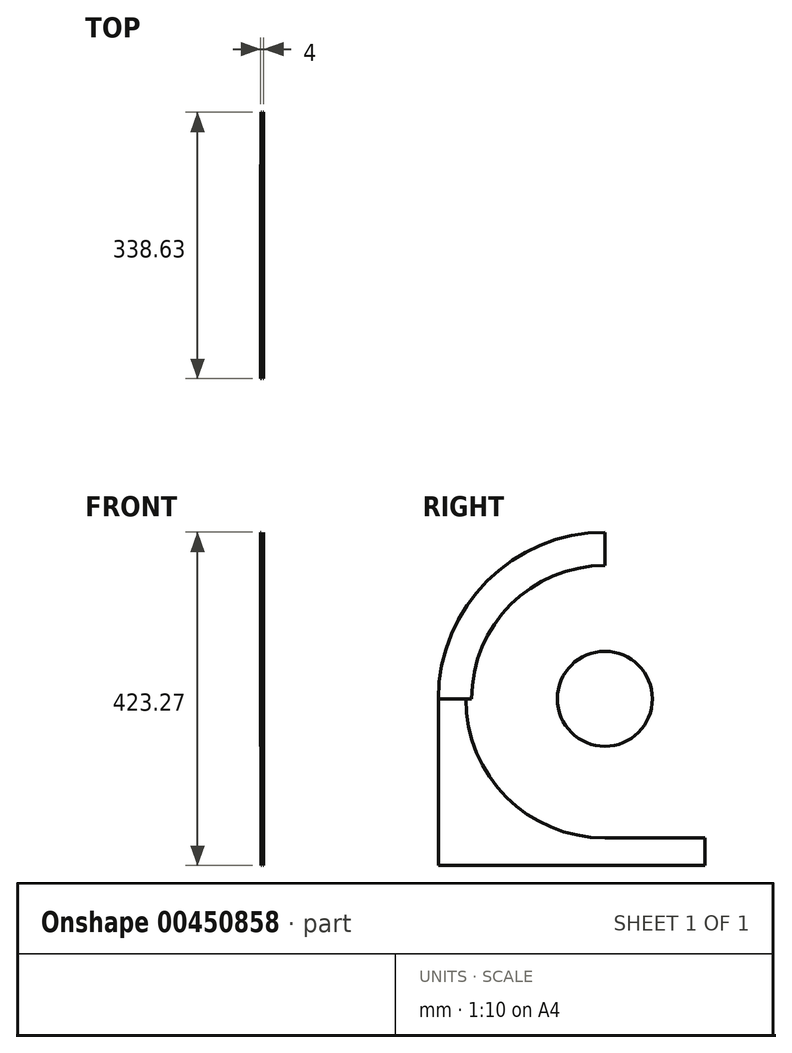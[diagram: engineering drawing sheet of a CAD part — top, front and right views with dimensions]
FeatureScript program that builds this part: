
annotation { "Feature Type Name" : "Feature", "Feature Type Description" : "" }
export const myFeature = defineFeature(function(context is Context, id is Id, definition is map)
    precondition{}
    {
        {
            assignVariable(context, id + "F0", {"name" : "trw", "anyValue" : .5});
        }
        {
            assignVariable(context, id + "F1", {"name" : "trsp", "anyValue" : 2});
        }
        {
            assignVariable(context, id + "F2", {"name" : "shwhw", "anyValue" : 1});
        }
        {
            var Q0;
            Q0=qCreatedBy(makeId("Right.planeOp"),FACE);
            cPlane(context, id + "F3", {"entities" : qUnion([Q0]), "cplaneType" : CPlaneType.OFFSET, "offset" : (getVariable(context, 'trsp') / 2) * mm, "width" : 152.4 * mm, "height" : 152.4 * mm});
        }
        {
            var Q0;
            Q0=qCreatedBy(id+"F3.planeOp",FACE);
            var sketch = newSketch(context, id + "F4", { "sketchPlane" : qUnion([Q0])});
            skLineSegment(sketch, "E0.bottom", {"start": v(0, 0) * mm, "end": v(127, 0) * mm});
            skLineSegment(sketch, "E0.top", {"start": v(0, 34.93) * mm, "end": v(127, 34.93) * mm});
            skLineSegment(sketch, "E0.left", {"start": v(0, 0) * mm, "end": v(0, 34.93) * mm});
            skLineSegment(sketch, "E0.right", {"start": v(127, 0) * mm, "end": v(127, 34.92) * mm});
            skCircle(sketch, "E1", {"center": v(0, 211.63) * mm, "radius": 60.33 * mm});
            skArc(sketch, "E2", {"start": v(-176.7, 211.63) * mm, "mid": v(-124.95, 86.68) * mm, "end": v(0, 34.93) * mm});
            skArc(sketch, "E3", {"start": v(-211.63, 211.63) * mm, "mid": v(-149.65, 61.99) * mm, "end": v(0, 0) * mm});
            skLineSegment(sketch, "E4", {"start": v(-176.7, 211.63) * mm, "end": v(-211.63, 211.63) * mm});
            skLineSegment(sketch, "E5", {"start": v(0, 0) * mm, "end": v(-211.63, 0) * mm});
            skLineSegment(sketch, "E6", {"start": v(-211.63, 0) * mm, "end": v(-211.63, 211.63) * mm});
            skSolve(sketch);
        }
        {
            var Q0;
            Q0=makeQuery(id+"F4.imprint","IMPRINT",FACE,{"disambiguationData":[TD([[makeQuery(id+"F4.imprint","IMPRINT",EDGE,{"derivedFrom":sQuery(id+"F4.wireOp",EDGE,"E1")}),1.0]])]});
            extrude(context, id + "F5", {"entities" : qUnion([Q0]), "depth" : (getVariable(context, 'shwhw')) * mm});
        }
        {
            var Q0;
            Q0=makeQuery(id+"F4.imprint","IMPRINT",FACE,{"disambiguationData":[TD([[makeQuery(id+"F4.imprint","IMPRINT",EDGE,{"derivedFrom":sQuery(id+"F4.wireOp",EDGE,"E0.left")}),1.0]])]});
            var Q1;
            Q1=makeQuery(id+"F4.imprint","IMPRINT",FACE,{"disambiguationData":[TD([[makeQuery(id+"F4.imprint","IMPRINT",EDGE,{"derivedFrom":sQuery(id+"F4.wireOp",EDGE,"E0.bottom")}),1.0]])]});
            extrude(context, id + "F6", {"entities" : qUnion([Q0, Q1]), "depth" : (getVariable(context, 'trw')) * mm});
        }
        {
            var Q0;
            Q0=makeQuery(id+"F4.imprint","IMPRINT",FACE,{"disambiguationData":[TD([[makeQuery(id+"F4.imprint","IMPRINT",EDGE,{"derivedFrom":sQuery(id+"F4.wireOp",EDGE,"E3")}),-1.0]])]});
            extrude(context, id + "F7", {"entities" : qUnion([Q0]), "operationType" : NewBodyOperationType.ADD, "depth" : (getVariable(context, 'trw')) * mm});
        }
        {
            var Q0;
            Q0=qCreatedBy(makeId("Right.planeOp"),FACE);
            cPlane(context, id + "F8", {"entities" : qUnion([Q0]), "cplaneType" : CPlaneType.OFFSET, "offset" : (getVariable(context, 'trsp') / 2 + getVariable(context, 'trw')) * mm, "width" : 152.4 * mm, "height" : 152.4 * mm});
        }
        {
            var Q0;
            Q0=qCreatedBy(id+"F8.planeOp",FACE);
            var sketch = newSketch(context, id + "F9", { "sketchPlane" : qUnion([Q0])});
            skCircle(sketch, "E7.0.0", {"center": v(0, 211.63) * mm, "radius": 60.33 * mm});
            skArc(sketch, "E8", {"start": v(0, 380.95) * mm, "mid": v(-119.72, 331.36) * mm, "end": v(-169.32, 211.63) * mm});
            skArc(sketch, "E9", {"start": v(0, 423.27) * mm, "mid": v(-149.65, 361.28) * mm, "end": v(-211.63, 211.63) * mm});
            skLineSegment(sketch, "E10", {"start": v(0, 423.27) * mm, "end": v(0, 380.95) * mm});
            skLineSegment(sketch, "E11", {"start": v(-169.32, 211.63) * mm, "end": v(-220.4, 211.63) * mm});
            skSolve(sketch);
        }
        {
            var Q0;
            {var subQ0=sQuery(id+"F9.wireOp",EDGE,"E8");Q0=makeQuery(id+"F9.imprint","IMPRINT",FACE,{"disambiguationData":[TD([[makeQuery(id+"F9.imprint","IMPRINT",EDGE,{"derivedFrom":subQ0}),-1.0]])]});}
            extrude(context, id + "F10", {"entities" : qUnion([Q0]), "depth" : (getVariable(context, 'trw')) * mm});
        }
        {
            var Q0;
            Q0=makeQuery(id+"F10.opExtrude","SWEPT_BODY",BODY,{"disambiguationData":[OSD([sQuery(id+"F9.wireOp",EDGE,"E8"),sQuery(id+"F9.wireOp",EDGE,"E9"),sQuery(id+"F9.wireOp",EDGE,"E10"),sQuery(id+"F9.wireOp",EDGE,"E11")])]});
            var Q1;
            Q1=makeQuery(id+"F5.opExtrude","SWEPT_BODY",BODY,{"disambiguationData":[OSD([sQuery(id+"F4.wireOp",EDGE,"E1")])]});
            var Q2;
            Q2=makeQuery(id+"F6.opExtrude","SWEPT_BODY",BODY,{"disambiguationData":[OSD([sQuery(id+"F4.wireOp",EDGE,"E0.bottom"),sQuery(id+"F4.wireOp",EDGE,"E0.top"),sQuery(id+"F4.wireOp",EDGE,"E0.right"),sQuery(id+"F4.wireOp",EDGE,"E2"),sQuery(id+"F4.wireOp",EDGE,"E3"),sQuery(id+"F4.wireOp",EDGE,"E4")])]});
            var Q3;
            Q3=qCreatedBy(makeId("Right.planeOp"),FACE);
            mirror(context, id + "F11", {"entities" : qUnion([Q0, Q1, Q2]), "mirrorPlane" : qUnion([Q3])});
        }
    });
